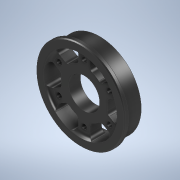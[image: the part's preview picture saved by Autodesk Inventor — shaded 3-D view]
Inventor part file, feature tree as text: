
AUTODESK INVENTOR PART (.ipt)
format: ipt  version: 2020 (Build 240168000, 168)  size: 292,864 bytes
history: native  units: in
note: dims shown in document units (in); Inventor stores cm internally (conversion verified against a paired STEP export)
features: sketch x3, revolve x1, extrude x1, pattern_circular x1, fillet x1, hole x1, chamfer x1
ambient origin geometry x8: Origin, YZ Plane, XZ Plane, XY Plane, X Axis, Y Axis, Z Axis, Center Point
bodies: Solid1 (feature_tree)
feature tree (9):
  revolve  "Revolution1"  [1 undecoded]
  extrude  "Extrusion1"  Depth=0.125in
  pattern_circular  "Circular Pattern1"  [2 undecoded]
  fillet  "Fillet1"  Radius=1.5in
  hole  "Hole1"  [1 undecoded]
  chamfer  "Chamfer1"  Distance=0.1875in
  sketch  "Sketch1"  dims[d0=1.4375in d1=0.25in]
  sketch  "Sketch2"  dims[d2=1.343in d3=0.125in]
  sketch  "Sketch3"  dims[d4=90.0deg d5=1.0in d6=1.5in d7=60.0deg d8=0.1875in d9=0.1875in d10=0.0in d11=0.0in d12=0.5in d13=0.125in d14=2.3622in d15=360.0deg d17=0.125in d18=1.875in d19=2.3622in d21=360.0deg d23=0.17in d24=0.75in d25=0.51in d26=0.188in d27=0.5635in d28=1.0in d29=0.8108in d30=0.0312in d31=0.125in d32=45.0deg]
note: 4 required parameter values undecoded (feature->parameter linkage not recoverable at this tier; creation-order binding heuristic only, values carry confidence <= 0.55)